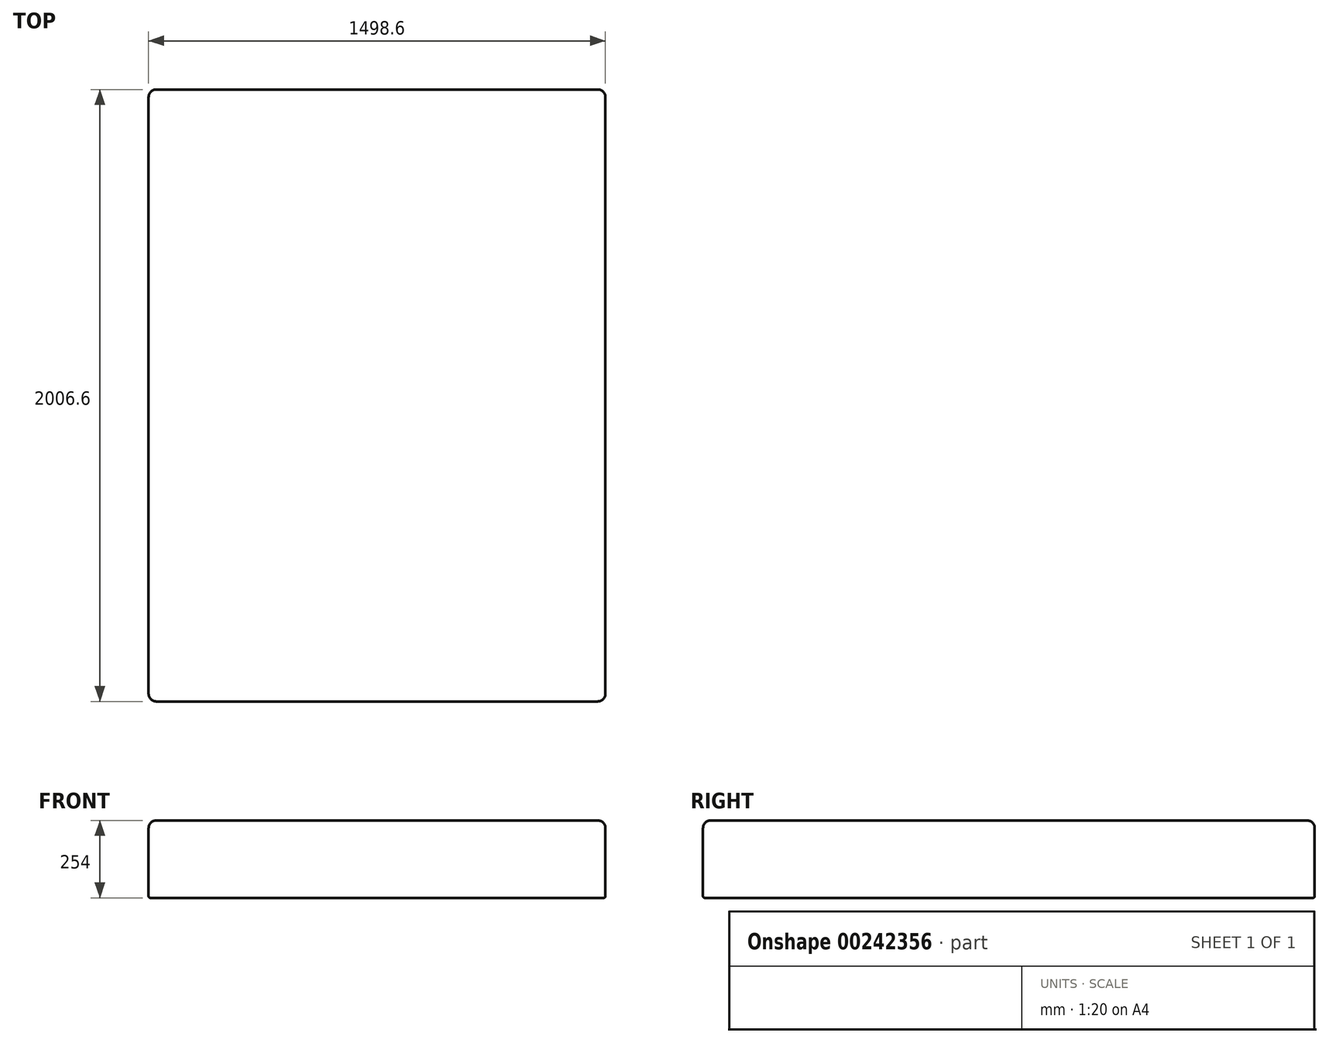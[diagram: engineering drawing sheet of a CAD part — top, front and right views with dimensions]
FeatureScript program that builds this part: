
annotation { "Feature Type Name" : "Feature", "Feature Type Description" : "" }
export const myFeature = defineFeature(function(context is Context, id is Id, definition is map)
    precondition{}
    {
        {
            var Q0;
            Q0=qCreatedBy(makeId("Top.planeOp"),FACE);
            var sketch = newSketch(context, id + "F0", { "sketchPlane" : qUnion([Q0])});
            skLineSegment(sketch, "E0.bottom", {"start": v(0, 0) * mm, "end": v(1498.6, 0) * mm});
            skLineSegment(sketch, "E0.top", {"start": v(0, 2006.6) * mm, "end": v(1498.6, 2006.6) * mm});
            skLineSegment(sketch, "E0.left", {"start": v(0, 0) * mm, "end": v(0, 2006.6) * mm});
            skLineSegment(sketch, "E0.right", {"start": v(1498.6, 0) * mm, "end": v(1498.6, 2006.6) * mm});
            skSolve(sketch);
        }
        {
            var Q0;
            Q0=makeQuery(id+"F0.imprint","IMPRINT",FACE,{"disambiguationData":[TD([[makeQuery(id+"F0.imprint","IMPRINT",EDGE,{"derivedFrom":sQuery(id+"F0.wireOp",EDGE,"E0.bottom")}),1.0]])]});
            extrude(context, id + "F1", {"entities" : qUnion([Q0]), "depth" : 254 * mm});
        }
        {
            var Q0;
            Q0=makeQuery(id+"F1.opExtrude","CAP_EDGE",EDGE,{"disambiguationData":[OSD([sQuery(id+"F0.wireOp",EDGE,"E0.left")])],"isStart":false});
            var Q1;
            Q1=makeQuery(id+"F1.opExtrude","CAP_EDGE",EDGE,{"disambiguationData":[OSD([sQuery(id+"F0.wireOp",EDGE,"E0.bottom")])],"isStart":false});
            var Q2;
            Q2=makeQuery(id+"F1.opExtrude","CAP_EDGE",EDGE,{"disambiguationData":[OSD([sQuery(id+"F0.wireOp",EDGE,"E0.right")])],"isStart":false});
            var Q3;
            Q3=makeQuery(id+"F1.opExtrude","CAP_EDGE",EDGE,{"disambiguationData":[OSD([sQuery(id+"F0.wireOp",EDGE,"E0.top")])],"isStart":false});
            var Q4;
            Q4=makeQuery(id+"F1.opExtrude","SWEPT_EDGE",EDGE,{"disambiguationData":[OSD([sQuery(id+"F0.wireOp",EDGE,"E0.bottom"),sQuery(id+"F0.wireOp",EDGE,"E0.right")])]});
            var Q5;
            Q5=makeQuery(id+"F1.opExtrude","SWEPT_EDGE",EDGE,{"disambiguationData":[OSD([sQuery(id+"F0.wireOp",EDGE,"E0.bottom"),sQuery(id+"F0.wireOp",EDGE,"E0.left")])]});
            var Q6;
            Q6=makeQuery(id+"F1.opExtrude","SWEPT_EDGE",EDGE,{"disambiguationData":[OSD([sQuery(id+"F0.wireOp",EDGE,"E0.top"),sQuery(id+"F0.wireOp",EDGE,"E0.right")])]});
            var Q7;
            Q7=makeQuery(id+"F1.opExtrude","SWEPT_EDGE",EDGE,{"disambiguationData":[OSD([sQuery(id+"F0.wireOp",EDGE,"E0.top"),sQuery(id+"F0.wireOp",EDGE,"E0.left")])]});
            fillet(context, id + "F2", {"entities" : qUnion([Q0, Q1, Q2, Q3, Q4, Q5, Q6, Q7]), "radius" : 25.4 * mm, "tangentPropagation" : true, "allowEdgeOverflow" : false});
        }
        {
            var Q0;
            Q0=makeQuery(id+"F1.opExtrude","CAP_EDGE",EDGE,{"disambiguationData":[OSD([sQuery(id+"F0.wireOp",EDGE,"E0.right")])],"isStart":true});
            var Q1;
            Q1=makeQuery(id+"F1.opExtrude","CAP_EDGE",EDGE,{"disambiguationData":[OSD([sQuery(id+"F0.wireOp",EDGE,"E0.bottom")])],"isStart":true});
            var Q2;
            Q2=makeQuery(id+"F1.opExtrude","CAP_EDGE",EDGE,{"disambiguationData":[OSD([sQuery(id+"F0.wireOp",EDGE,"E0.left")])],"isStart":true});
            var Q3;
            Q3=makeQuery(id+"F1.opExtrude","CAP_EDGE",EDGE,{"disambiguationData":[OSD([sQuery(id+"F0.wireOp",EDGE,"E0.top")])],"isStart":true});
            fillet(context, id + "F3", {"entities" : qUnion([Q0, Q1, Q2, Q3]), "radius" : 5.08 * mm, "tangentPropagation" : true, "allowEdgeOverflow" : false});
        }
    });
